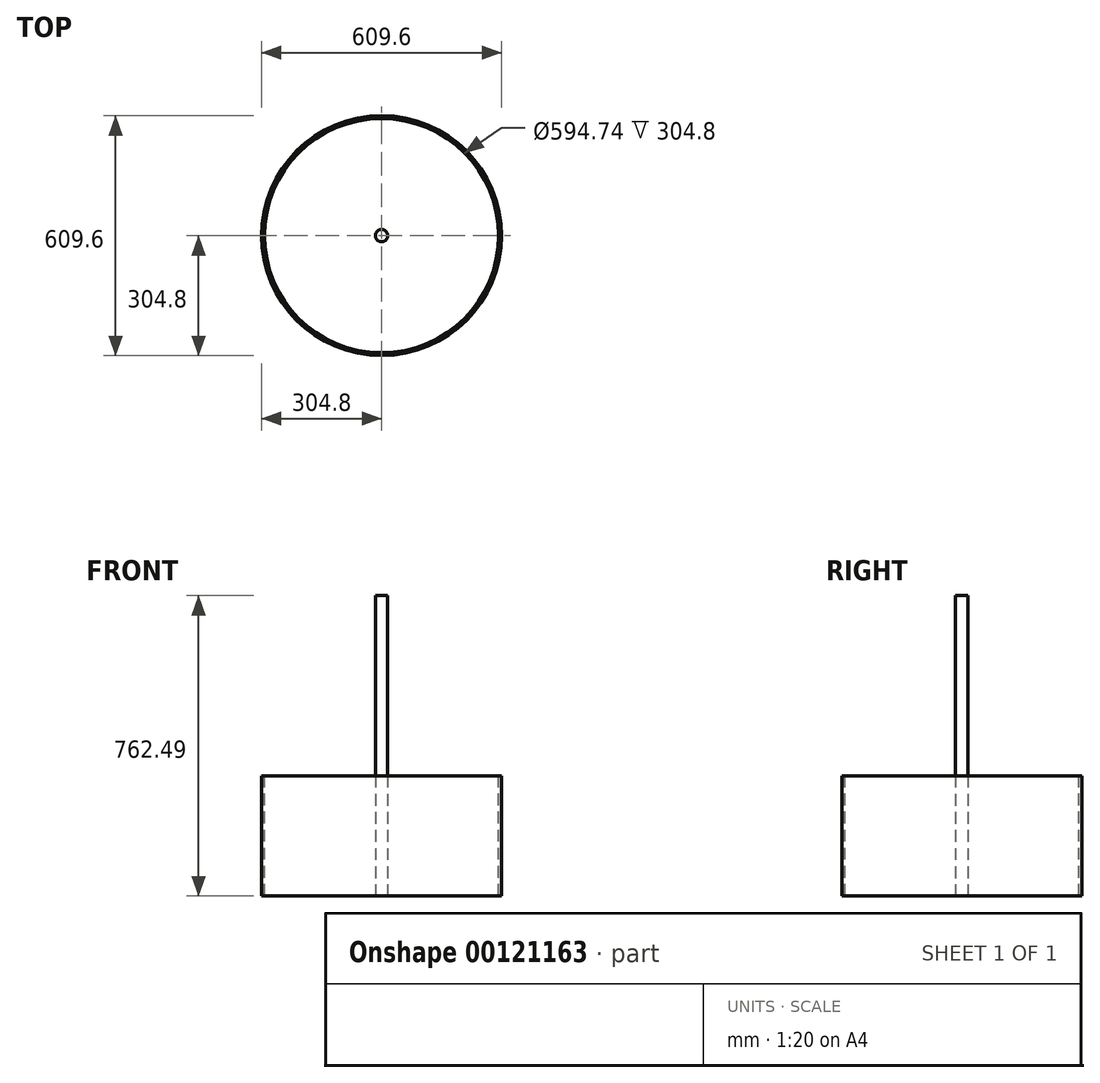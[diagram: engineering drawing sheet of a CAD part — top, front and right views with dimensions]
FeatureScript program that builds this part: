
annotation { "Feature Type Name" : "Feature", "Feature Type Description" : "" }
export const myFeature = defineFeature(function(context is Context, id is Id, definition is map)
    precondition{}
    {
        {
            var Q0;
            Q0=qCreatedBy(makeId("Top.planeOp"),FACE);
            var sketch = newSketch(context, id + "F0", { "sketchPlane" : qUnion([Q0])});
            skCircle(sketch, "E0", {"center": v(0, 0) * mm, "radius": 304.8 * mm});
            skSolve(sketch);
        }
        {
            var Q0;
            Q0=makeQuery(id+"F0.imprint","IMPRINT",FACE,{"disambiguationData":[TD([[makeQuery(id+"F0.imprint","IMPRINT",EDGE,{"derivedFrom":sQuery(id+"F0.wireOp",EDGE,"E0")}),1.0]])]});
            extrude(context, id + "F1", {"entities" : qUnion([Q0]), "depth" : 304.8 * mm});
        }
        {
            var Q0;
            Q0=makeQuery(id+"F1.opExtrude","CAP_FACE",FACE,{"disambiguationData":[OSD([sQuery(id+"F0.wireOp",EDGE,"E0")])],"isStart":false});
            var sketch = newSketch(context, id + "F2", { "sketchPlane" : qUnion([Q0])});
            skCircle(sketch, "E1", {"center": v(0, 0) * mm, "radius": 297.37 * mm});
            skSolve(sketch);
        }
        {
            var Q0;
            Q0=sQuery(id+"F2.wireOp",VERTEX,"E1.center");
            var Q1;
            Q1=makeQuery(id+"F1.opExtrude","SWEPT_BODY",BODY,{"disambiguationData":[OSD([sQuery(id+"F0.wireOp",EDGE,"E0")])]});
            hole(context, id + "F3", {"style" : HoleStyle.SIMPLE, "endStyle" : HoleEndStyle.THROUGH, "holeDiameter" : 594.74 * mm, "locations" : qUnion([Q0]), "scope" : qUnion([Q1]), "isTappedThrough" : true});
        }
        {
            var Q0;
            Q0=makeQuery(id+"F1.opExtrude","CAP_FACE",FACE,{"disambiguationData":[OSD([sQuery(id+"F0.wireOp",EDGE,"E0")])],"isStart":true});
            var sketch = newSketch(context, id + "F4", { "sketchPlane" : qUnion([Q0])});
            skCircle(sketch, "E2", {"center": v(0, 0) * mm, "radius": 15.54 * mm});
            skSolve(sketch);
        }
        {
            var Q0;
            Q0 = qSketchRegion(id + "F4", true);
            extrude(context, id + "F5", {"entities" : qUnion([Q0]), "oppositeDirection" : true, "depth" : 762.5 * mm});
        }
    });
